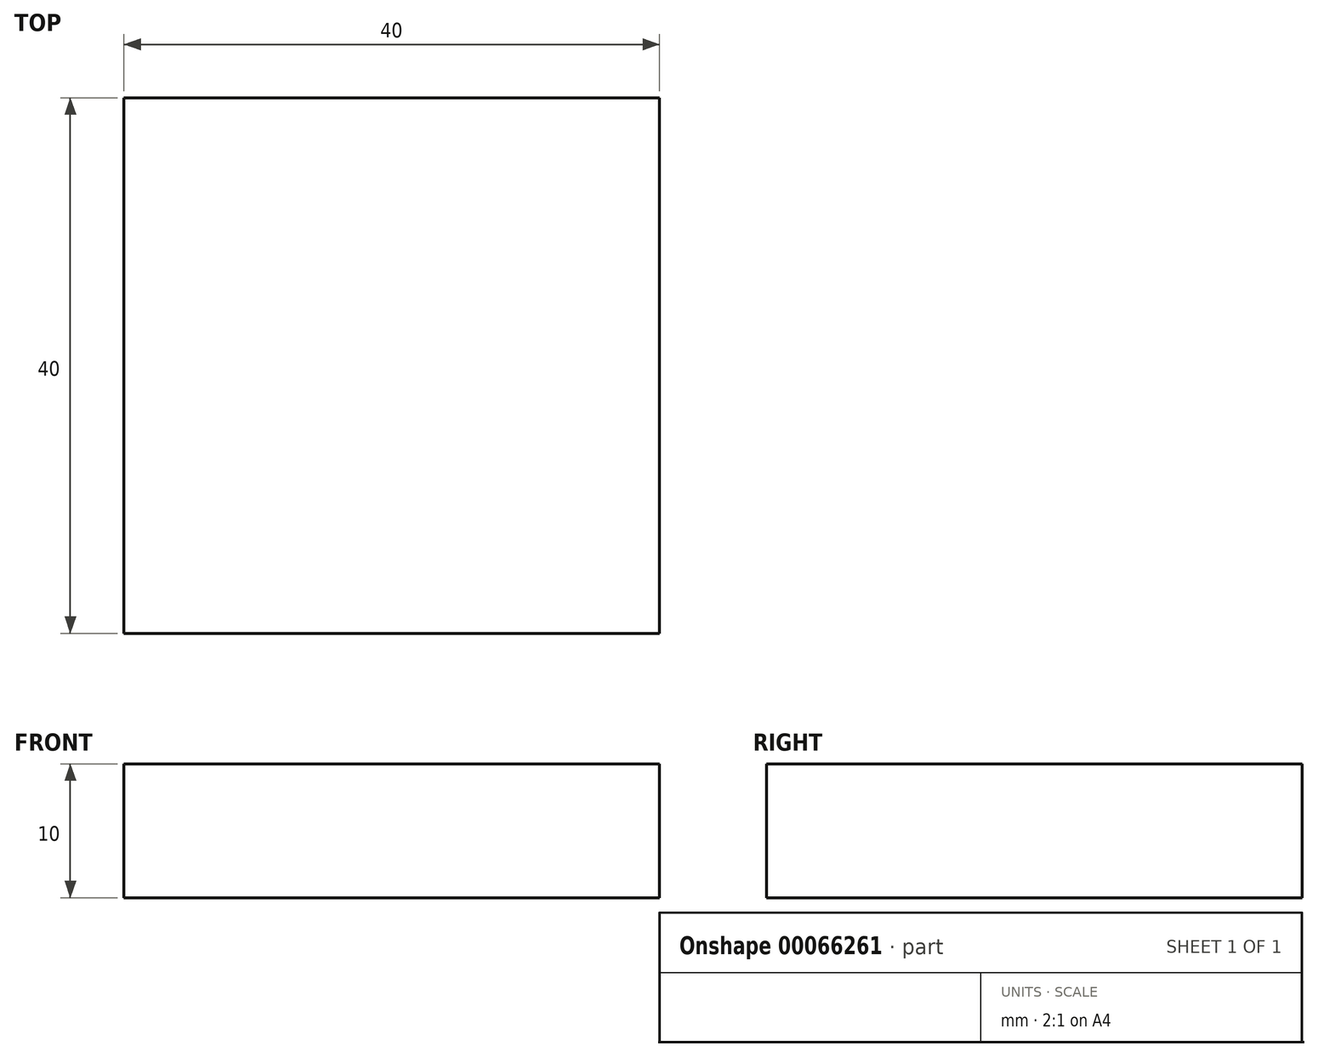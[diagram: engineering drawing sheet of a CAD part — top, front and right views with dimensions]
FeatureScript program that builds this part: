
annotation { "Feature Type Name" : "Feature", "Feature Type Description" : "" }
export const myFeature = defineFeature(function(context is Context, id is Id, definition is map)
    precondition{}
    {
        {
            var Q0;
            Q0=qCreatedBy(makeId("Top.planeOp"),FACE);
            var sketch = newSketch(context, id + "F0", { "sketchPlane" : qUnion([Q0])});
            skLineSegment(sketch, "E0.bottom", {"start": v(-15.53, 20.03) * mm, "end": v(24.47, 20.03) * mm});
            skLineSegment(sketch, "E0.top", {"start": v(-15.53, -19.97) * mm, "end": v(24.47, -19.97) * mm});
            skLineSegment(sketch, "E0.left", {"start": v(-15.53, 20.03) * mm, "end": v(-15.53, -19.97) * mm});
            skLineSegment(sketch, "E0.right", {"start": v(24.47, 20.03) * mm, "end": v(24.47, -19.97) * mm});
            skSolve(sketch);
        }
        {
            var Q0;
            Q0 = qSketchRegion(id + "F0", true);
            var Q1;
            Q1=makeQuery(id+"F0.imprint","IMPRINT",FACE,{"disambiguationData":[TD([[makeQuery(id+"F0.imprint","IMPRINT",EDGE,{"derivedFrom":sQuery(id+"F0.wireOp",EDGE,"E0.bottom")}),-1.0]])]});
            extrude(context, id + "F1", {"entities" : qUnion([Q0, Q1]), "depth" : 10 * mm});
        }
    });
